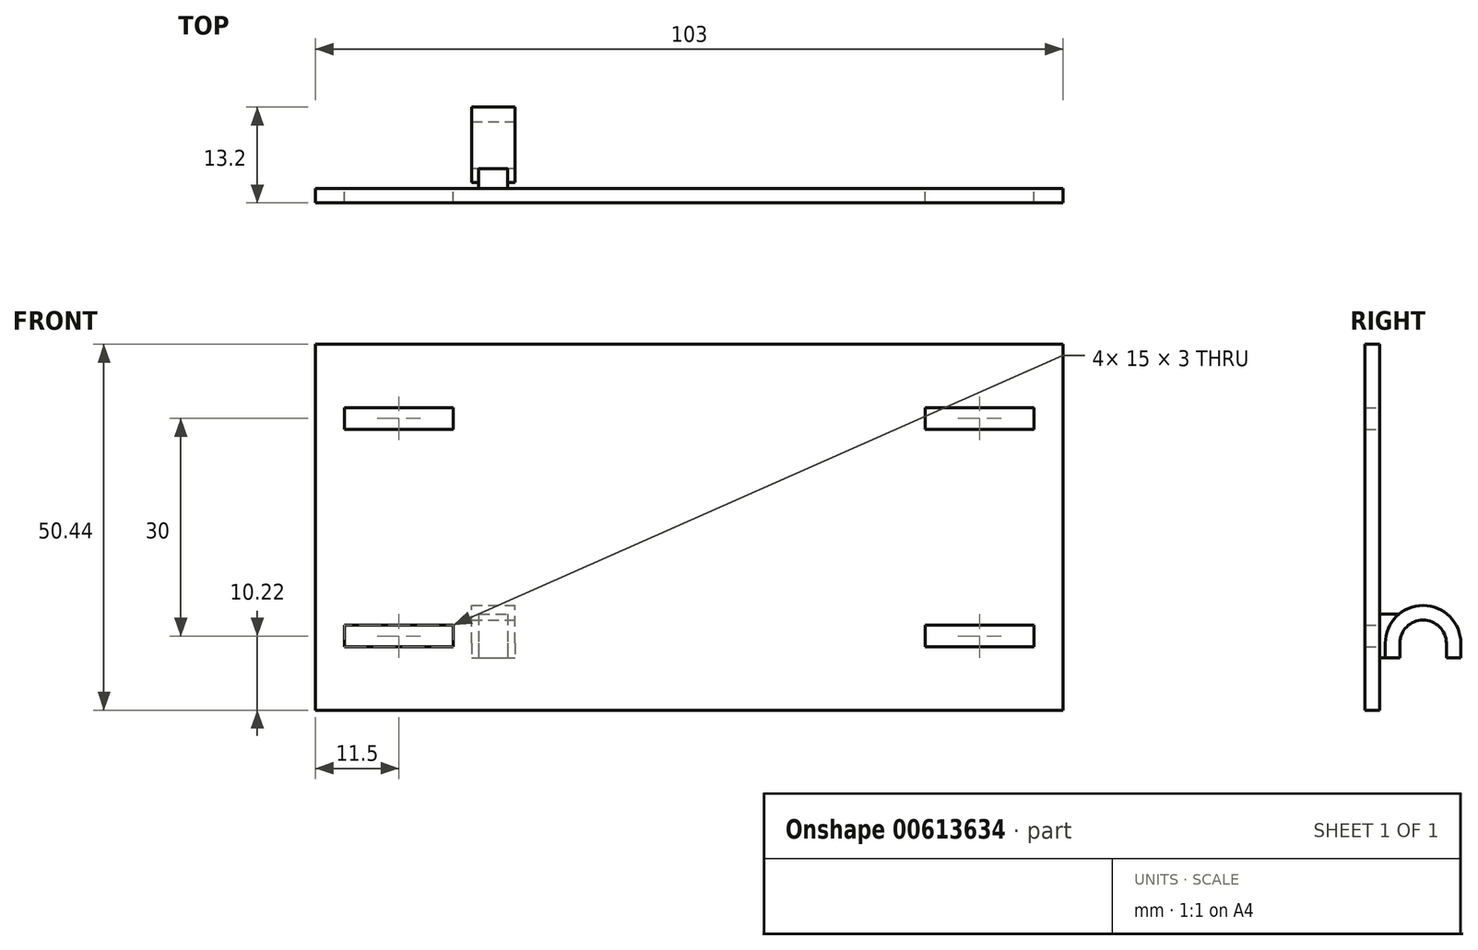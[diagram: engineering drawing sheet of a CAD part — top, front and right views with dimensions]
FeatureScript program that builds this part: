
annotation { "Feature Type Name" : "Feature", "Feature Type Description" : "" }
export const myFeature = defineFeature(function(context is Context, id is Id, definition is map)
    precondition{}
    {
        {
            var Q0;
            Q0=qCreatedBy(makeId("Front.planeOp"),FACE);
            var sketch = newSketch(context, id + "F0", { "sketchPlane" : qUnion([Q0])});
            skLineSegment(sketch, "E0.bottom", {"start": v(-51.5, -15.22) * mm, "end": v(51.5, -15.22) * mm});
            skLineSegment(sketch, "E0.top", {"start": v(-51.5, 35.22) * mm, "end": v(51.5, 35.22) * mm});
            skLineSegment(sketch, "E0.left", {"start": v(-51.5, -15.22) * mm, "end": v(-51.5, 35.22) * mm});
            skLineSegment(sketch, "E0.right", {"start": v(51.5, -15.22) * mm, "end": v(51.5, 35.22) * mm});
            skPoint(sketch, "E0.middle", {"position": v(0, 10) * mm});
            skLineSegment(sketch, "E1", {"start": v(18.15, 40) * mm, "end": v(-18.15, 40) * mm});
            skLineSegment(sketch, "E2.bottom", {"start": v(32.5, -6.5) * mm, "end": v(47.5, -6.5) * mm});
            skLineSegment(sketch, "E2.top", {"start": v(32.5, -3.5) * mm, "end": v(47.5, -3.5) * mm});
            skLineSegment(sketch, "E2.left", {"start": v(32.5, -6.5) * mm, "end": v(32.5, -3.5) * mm});
            skLineSegment(sketch, "E2.right", {"start": v(47.5, -6.5) * mm, "end": v(47.5, -3.5) * mm});
            skPoint(sketch, "E2.middle", {"position": v(40, -5) * mm});
            skLineSegment(sketch, "E3.bottom", {"start": v(-47.5, -6.5) * mm, "end": v(-32.5, -6.5) * mm});
            skLineSegment(sketch, "E3.top", {"start": v(-47.5, -3.5) * mm, "end": v(-32.5, -3.5) * mm});
            skLineSegment(sketch, "E3.left", {"start": v(-47.5, -6.5) * mm, "end": v(-47.5, -3.5) * mm});
            skLineSegment(sketch, "E3.right", {"start": v(-32.5, -6.5) * mm, "end": v(-32.5, -3.5) * mm});
            skPoint(sketch, "E3.middle", {"position": v(-40, -5) * mm});
            skPoint(sketch, "E3.middle.positionSnap0", {"position": v(32.5, -5) * mm});
            skPoint(sketch, "E3.centerSnap0", {"position": v(32.5, -5) * mm});
            skLineSegment(sketch, "E4.bottom", {"start": v(-47.5, 23.5) * mm, "end": v(-32.5, 23.5) * mm});
            skLineSegment(sketch, "E4.top", {"start": v(-47.5, 26.5) * mm, "end": v(-32.5, 26.5) * mm});
            skLineSegment(sketch, "E4.left", {"start": v(-47.5, 23.5) * mm, "end": v(-47.5, 26.5) * mm});
            skLineSegment(sketch, "E4.right", {"start": v(-32.5, 23.5) * mm, "end": v(-32.5, 26.5) * mm});
            skPoint(sketch, "E4.middle", {"position": v(-40, 25) * mm});
            skLineSegment(sketch, "E5.bottom", {"start": v(32.5, 23.5) * mm, "end": v(47.5, 23.5) * mm});
            skLineSegment(sketch, "E5.top", {"start": v(32.5, 26.5) * mm, "end": v(47.5, 26.5) * mm});
            skLineSegment(sketch, "E5.left", {"start": v(32.5, 23.5) * mm, "end": v(32.5, 26.5) * mm});
            skLineSegment(sketch, "E5.right", {"start": v(47.5, 23.5) * mm, "end": v(47.5, 26.5) * mm});
            skPoint(sketch, "E5.middle", {"position": v(40, 25) * mm});
            skPoint(sketch, "E5.middle.positionSnap0", {"position": v(-32.5, 25) * mm});
            skPoint(sketch, "E5.centerSnap0", {"position": v(-32.5, 25) * mm});
            skPoint(sketch, "E6", {"position": v(0, 40) * mm});
            skSolve(sketch);
        }
        {
            var Q0;
            Q0 = qSketchRegion(id + "F0", true);
            extrude(context, id + "F1", {"entities" : qUnion([Q0]), "depth" : 2 * mm, "offsetDistance" : 25 * mm});
        }
        {
            var Q0;
            Q0=qCreatedBy(makeId("Right.planeOp"),FACE);
            var sketch = newSketch(context, id + "F2", { "sketchPlane" : qUnion([Q0])});
            skLineSegment(sketch, "E7", {"start": v(9.2, -8) * mm, "end": v(9.2, -6) * mm});
            skArc(sketch, "E8", {"start": v(9.2, -6) * mm, "mid": v(6, -2.8) * mm, "end": v(2.8, -6) * mm});
            skLineSegment(sketch, "E9", {"start": v(2.8, -6) * mm, "end": v(2.8, -8) * mm});
            skLineSegment(sketch, "E10", {"start": v(11.2, -8) * mm, "end": v(11.2, -6) * mm});
            skArc(sketch, "E11", {"start": v(11.2, -6) * mm, "mid": v(6, -0.8) * mm, "end": v(0.8, -6) * mm});
            skLineSegment(sketch, "E12", {"start": v(0.8, -6) * mm, "end": v(0.8, -8) * mm});
            skLineSegment(sketch, "E13", {"start": v(2.8, -8) * mm, "end": v(0.8, -8) * mm});
            skLineSegment(sketch, "E14", {"start": v(9.2, -8) * mm, "end": v(11.2, -8) * mm});
            skLineSegment(sketch, "E15", {"start": v(0, -8) * mm, "end": v(0.8, -8) * mm});
            skLineSegment(sketch, "E16", {"start": v(0, -2) * mm, "end": v(2.68, -2) * mm});
            skLineSegment(sketch, "E17", {"start": v(0, -2) * mm, "end": v(0, -8) * mm});
            skSolve(sketch);
        }
        {
            var Q0;
            Q0=makeQuery(id+"F2.imprint","IMPRINT",FACE,{"disambiguationData":[TD([[makeQuery(id+"F2.imprint","IMPRINT",EDGE,{"derivedFrom":sQuery(id+"F2.wireOp",EDGE,"E7")}),-1.0]])]});
            extrude(context, id + "F3", {"entities" : qUnion([Q0]), "operationType" : NewBodyOperationType.ADD, "oppositeDirection" : true, "depth" : 30 * mm, "offsetDistance" : 25 * mm, "hasSecondDirection" : true, "secondDirectionOppositeDirection" : true, "secondDirectionDepth" : 24 * mm});
        }
        {
            var Q0;
            {var subQ0=sQuery(id+"F2.wireOp",EDGE,"E12");Q0=makeQuery(id+"F2.imprint","IMPRINT",FACE,{"disambiguationData":[TD([[makeQuery(id+"F2.imprint","IMPRINT",EDGE,{"derivedFrom":subQ0}),-1.0]])]});}
            extrude(context, id + "F4", {"entities" : qUnion([Q0]), "operationType" : NewBodyOperationType.ADD, "oppositeDirection" : true, "depth" : 29 * mm, "offsetDistance" : 25 * mm, "hasSecondDirection" : true, "secondDirectionOppositeDirection" : true, "secondDirectionDepth" : 25 * mm});
        }
        {
            var Q0;
            Q0=sQuery(id+"F0.wireOp",VERTEX,"E1.start");
            var Q1;
            Q1=sQuery(id+"F0.wireOp",VERTEX,"E1.end");
            var Q2;
            Q2=makeQuery(id+"F1.opExtrude","SWEPT_BODY",BODY,{"disambiguationData":[OSD([sQuery(id+"F0.wireOp",EDGE,"E0.bottom"),sQuery(id+"F0.wireOp",EDGE,"E0.top"),sQuery(id+"F0.wireOp",EDGE,"E0.left"),sQuery(id+"F0.wireOp",EDGE,"E0.right"),sQuery(id+"F0.wireOp",EDGE,"E2.bottom"),sQuery(id+"F0.wireOp",EDGE,"E2.top"),sQuery(id+"F0.wireOp",EDGE,"E2.left"),sQuery(id+"F0.wireOp",EDGE,"E2.right"),sQuery(id+"F0.wireOp",EDGE,"E3.bottom"),sQuery(id+"F0.wireOp",EDGE,"E3.top"),sQuery(id+"F0.wireOp",EDGE,"E3.left"),sQuery(id+"F0.wireOp",EDGE,"E3.right"),sQuery(id+"F0.wireOp",EDGE,"E4.bottom"),sQuery(id+"F0.wireOp",EDGE,"E4.top"),sQuery(id+"F0.wireOp",EDGE,"E4.left"),sQuery(id+"F0.wireOp",EDGE,"E4.right"),sQuery(id+"F0.wireOp",EDGE,"E5.bottom"),sQuery(id+"F0.wireOp",EDGE,"E5.top"),sQuery(id+"F0.wireOp",EDGE,"E5.left"),sQuery(id+"F0.wireOp",EDGE,"E5.right")])]});
            hole(context, id + "F5", {"style" : HoleStyle.SIMPLE, "endStyle" : HoleEndStyle.BLIND, "oppositeDirection" : true, "holeDiameter" : 3.2 * mm, "majorDiameter" : 5 * mm, "holeDepth" : 60 * mm, "isTappedThrough" : true, "tappedDepth" : 2.3 * mm, "tapClearance" : 3, "startFromSketch" : true, "locations" : qUnion([Q0, Q1]), "scope" : qUnion([Q2])});
        }
    });
